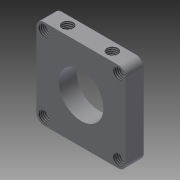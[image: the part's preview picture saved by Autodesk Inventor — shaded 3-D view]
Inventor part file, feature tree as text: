
AUTODESK INVENTOR PART (.ipt)
format: ipt  version: 2013 (Build 170138000, 138)  size: 159,744 bytes
history: native  units: in
note: dims shown in document units (in); Inventor stores cm internally (conversion verified against a paired STEP export)
features: thread x8, extrude x3, sketch x3, fillet x1
ambient origin geometry x8: Origin, YZ Plane, XZ Plane, XY Plane, X Axis, Y Axis, Z Axis, Center Point
bodies: Solid1 (feature_tree)
feature tree (15):
  extrude  "Extrusion1"  Depth=1.5in
  fillet  "Fillet1"  Radius=0.185in
  extrude  "Extrusion2"  Depth=0.125in
  extrude  "Extrusion3"  Depth=0.75in
  thread  "Thread1"  [1 undecoded]
  thread  "Thread2"  [1 undecoded]
  thread  "Thread3"  [1 undecoded]
  thread  "Thread4"  [1 undecoded]
  thread  "Thread5"  [1 undecoded]
  thread  "Thread6"  [1 undecoded]
  thread  "Thread7"  [1 undecoded]
  thread  "Thread8"  [1 undecoded]
  sketch  "Sketch1"  dims[d0=1.5in d1=1.5in d2=0.185in]
  sketch  "Sketch2"  dims[d3=0.7874in d5=1.25in d6=0.7874in d8=1.25in d11=0.125in]
  sketch  "Sketch3"  dims[d12=0.125in d13=0.75in d14=0.75in d15=0.5in d16=0.125in d17=0.125in d18=0.075in d22=1.5748in d24=360.0deg d26=0.3in d27=0.0in d28=0.125in d29=0.15in d30=0.375in d31=0.375in d32=0.185in d33=0.185in d34=0.3in d35=0.0in d36=0.15in d37=0.375in d38=0.375in d39=0.185in d40=0.185in d41=0.3in d42=0.0in d43=1.0in d44=0.0in d45=1.0in d46=0.0in d47=1.0in d48=0.0in d49=1.0in d50=0.0in d51=1.0in d52=0.0in d53=1.0in d54=0.0in d55=1.0in d56=0.0in d57=1.0in d58=0.0in]
note: 8 required parameter values undecoded (feature->parameter linkage not recoverable at this tier; creation-order binding heuristic only, values carry confidence <= 0.55)
